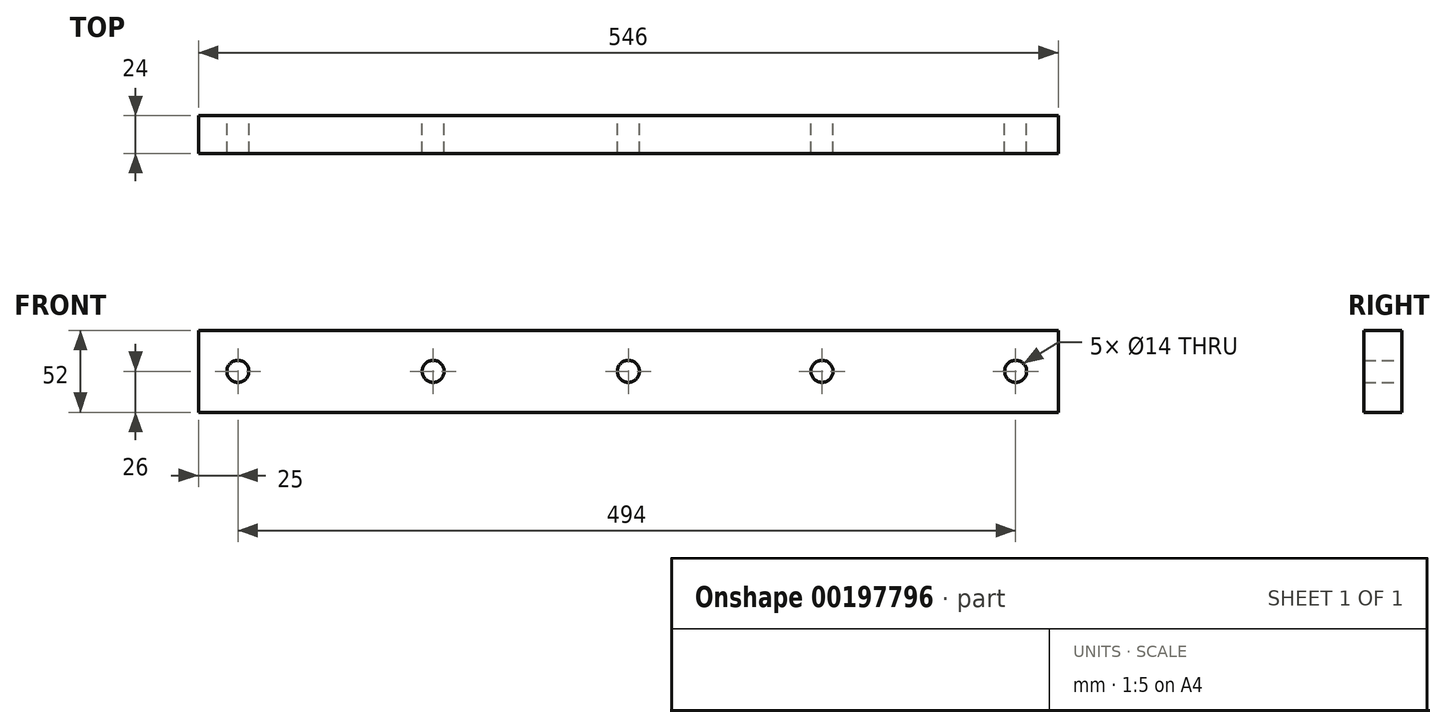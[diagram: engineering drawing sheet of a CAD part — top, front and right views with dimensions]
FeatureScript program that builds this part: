
annotation { "Feature Type Name" : "Feature", "Feature Type Description" : "" }
export const myFeature = defineFeature(function(context is Context, id is Id, definition is map)
    precondition{}
    {
        {
            var Q0;
            Q0=qCreatedBy(makeId("Front.planeOp"),FACE);
            var sketch = newSketch(context, id + "F0", { "sketchPlane" : qUnion([Q0])});
            skLineSegment(sketch, "E0.bottom", {"start": v(-273, 26) * mm, "end": v(273, 26) * mm});
            skLineSegment(sketch, "E0.top", {"start": v(-273, -26) * mm, "end": v(273, -26) * mm});
            skLineSegment(sketch, "E0.left", {"start": v(-273, 26) * mm, "end": v(-273, -26) * mm});
            skLineSegment(sketch, "E0.right", {"start": v(273, 26) * mm, "end": v(273, -26) * mm});
            skPoint(sketch, "E0.middle", {"position": v(0, 0) * mm});
            skCircle(sketch, "E1", {"center": v(-124, 0) * mm, "radius": 7 * mm});
            skCircle(sketch, "E2", {"center": v(-248, 0) * mm, "radius": 7 * mm});
            skCircle(sketch, "E3", {"center": v(0, 0) * mm, "radius": 7 * mm});
            skCircle(sketch, "E4", {"center": v(246, 0) * mm, "radius": 7 * mm});
            skPoint(sketch, "E5.endSnap0", {"position": v(273, 0) * mm});
            skCircle(sketch, "E6", {"center": v(123, 0) * mm, "radius": 7 * mm});
            skSolve(sketch);
        }
        {
            var Q0;
            Q0 = qSketchRegion(id + "F0", true);
            extrude(context, id + "F1", {"entities" : qUnion([Q0]), "depth" : 24 * mm});
        }
    });
